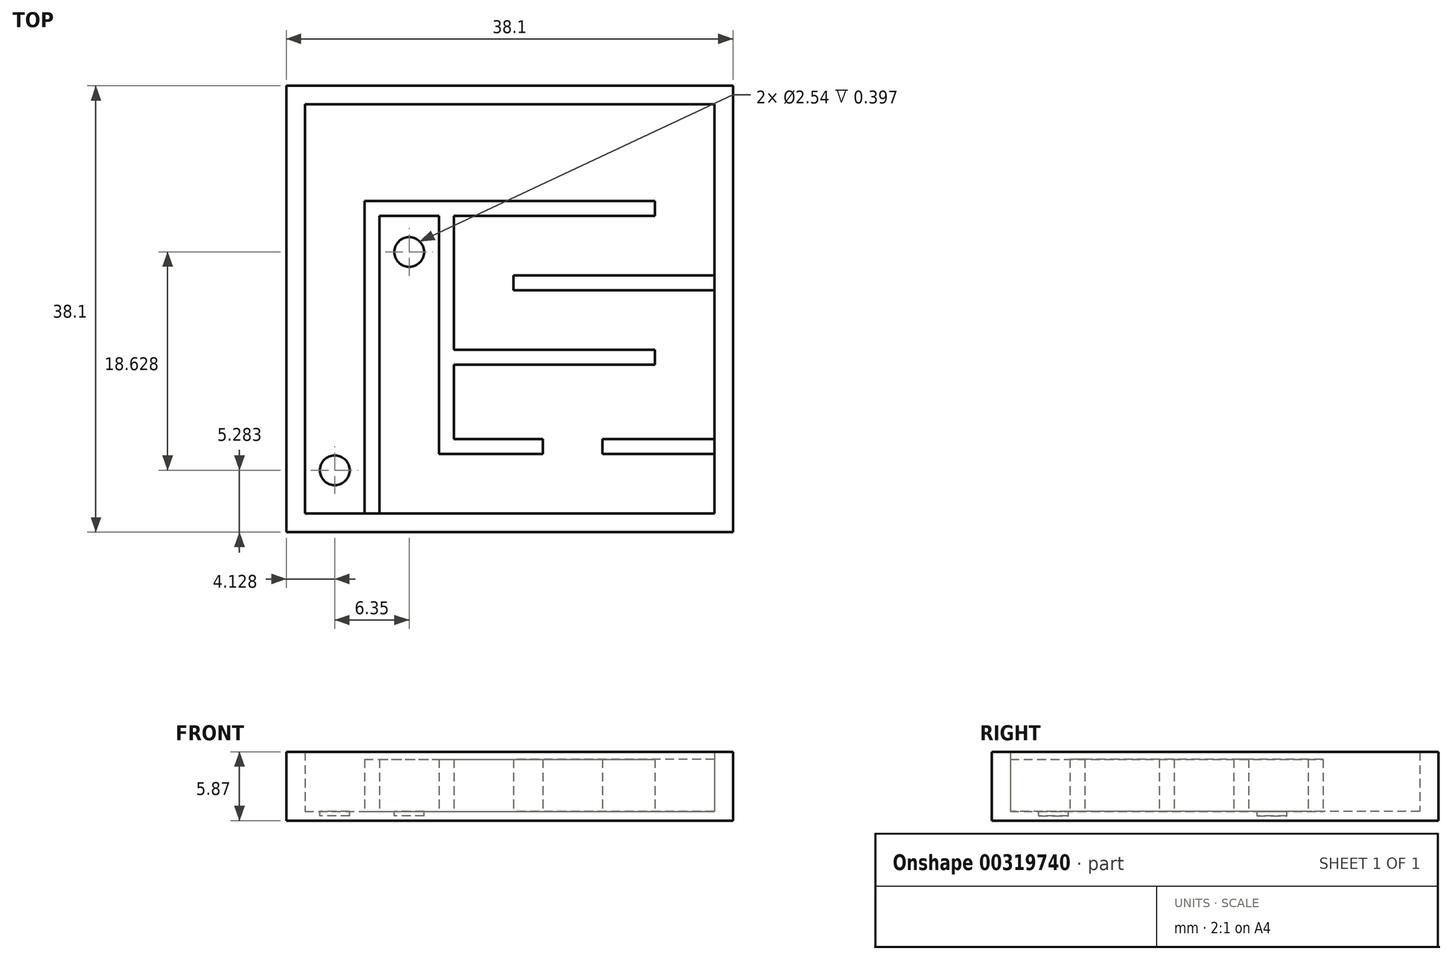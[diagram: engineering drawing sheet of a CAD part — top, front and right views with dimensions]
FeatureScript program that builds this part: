
annotation { "Feature Type Name" : "Feature", "Feature Type Description" : "" }
export const myFeature = defineFeature(function(context is Context, id is Id, definition is map)
    precondition{}
    {
        {
            var Q0;
            Q0=qCreatedBy(makeId("Top.planeOp"),FACE);
            var sketch = newSketch(context, id + "F0", { "sketchPlane" : qUnion([Q0])});
            skLineSegment(sketch, "E0.bottom", {"start": v(-12.95, 15.4) * mm, "end": v(25.15, 15.4) * mm});
            skLineSegment(sketch, "E0.top", {"start": v(-12.95, -22.7) * mm, "end": v(25.15, -22.7) * mm});
            skLineSegment(sketch, "E0.left", {"start": v(-12.95, 15.4) * mm, "end": v(-12.95, -22.7) * mm});
            skLineSegment(sketch, "E0.right", {"start": v(25.15, 15.4) * mm, "end": v(25.15, -22.7) * mm});
            skSolve(sketch);
        }
        {
            var Q0;
            Q0=makeQuery(id+"F0.imprint","IMPRINT",FACE,{"disambiguationData":[TD([[makeQuery(id+"F0.imprint","IMPRINT",EDGE,{"derivedFrom":sQuery(id+"F0.wireOp",EDGE,"E0.bottom")}),-1.0]])]});
            extrude(context, id + "F1", {"entities" : qUnion([Q0]), "depth" : 0.8 * mm});
        }
        {
            var Q0;
            Q0=makeQuery(id+"F1.opExtrude","CAP_FACE",FACE,{"disambiguationData":[OSD([sQuery(id+"F0.wireOp",EDGE,"E0.bottom"),sQuery(id+"F0.wireOp",EDGE,"E0.top"),sQuery(id+"F0.wireOp",EDGE,"E0.left"),sQuery(id+"F0.wireOp",EDGE,"E0.right")])],"isStart":false});
            var sketch = newSketch(context, id + "F2", { "sketchPlane" : qUnion([Q0])});
            skLineSegment(sketch, "E1.0", {"start": v(-11.36, 13.8) * mm, "end": v(23.56, 13.8) * mm});
            skLineSegment(sketch, "E1.1", {"start": v(-11.36, 13.8) * mm, "end": v(-11.36, -21.12) * mm});
            skLineSegment(sketch, "E1.2", {"start": v(-11.36, -21.12) * mm, "end": v(23.56, -21.12) * mm});
            skLineSegment(sketch, "E1.3", {"start": v(23.56, 13.8) * mm, "end": v(23.56, -21.12) * mm});
            skSolve(sketch);
        }
        {
            var Q0;
            Q0=makeQuery(id+"F2.imprint","IMPRINT",FACE,{"disambiguationData":[TD([[makeQuery(id+"F2.imprint","IMPRINT",EDGE,{"derivedFrom":sQuery(id+"F2.wireOp",EDGE,"E1.0")}),1.0]])]});
            extrude(context, id + "F3", {"entities" : qUnion([Q0]), "operationType" : NewBodyOperationType.ADD, "depth" : 5.08 * mm});
        }
        {
            var Q0;
            Q0=makeQuery(id+"F1.opExtrude","CAP_FACE",FACE,{"disambiguationData":[OSD([sQuery(id+"F0.wireOp",EDGE,"E0.bottom"),sQuery(id+"F0.wireOp",EDGE,"E0.top"),sQuery(id+"F0.wireOp",EDGE,"E0.left"),sQuery(id+"F0.wireOp",EDGE,"E0.right")])],"isStart":false});
            var sketch = newSketch(context, id + "F4", { "sketchPlane" : qUnion([Q0])});
            skLineSegment(sketch, "E2.bottom", {"start": v(-6.28, -21.12) * mm, "end": v(-5.01, -21.12) * mm});
            skLineSegment(sketch, "E2.top", {"start": v(-6.28, 5.55) * mm, "end": v(-5.01, 5.55) * mm});
            skLineSegment(sketch, "E2.left", {"start": v(-6.28, -21.12) * mm, "end": v(-6.28, 5.55) * mm});
            skLineSegment(sketch, "E2.right", {"start": v(-5.01, -21.12) * mm, "end": v(-5.01, 4.28) * mm});
            skLineSegment(sketch, "E3.bottom", {"start": v(-5.01, 5.55) * mm, "end": v(18.48, 5.55) * mm});
            skLineSegment(sketch, "E3.top", {"start": v(-5.01, 4.28) * mm, "end": v(0.07, 4.28) * mm});
            skLineSegment(sketch, "E3.right", {"start": v(18.48, 5.55) * mm, "end": v(18.48, 4.28) * mm});
            skLineSegment(sketch, "E4.left", {"start": v(0.07, 4.28) * mm, "end": v(0.07, -16.04) * mm});
            skLineSegment(sketch, "E4.right", {"start": v(1.34, 4.28) * mm, "end": v(1.34, -7.15) * mm});
            skLineSegment(sketch, "E5.bottom", {"start": v(1.34, -7.15) * mm, "end": v(18.48, -7.15) * mm});
            skLineSegment(sketch, "E5.top", {"start": v(1.34, -8.42) * mm, "end": v(18.48, -8.42) * mm});
            skLineSegment(sketch, "E5.right", {"start": v(18.48, -7.15) * mm, "end": v(18.48, -8.42) * mm});
            skLineSegment(sketch, "E6.top", {"start": v(1.34, -14.77) * mm, "end": v(8.93, -14.77) * mm});
            skLineSegment(sketch, "E6.right", {"start": v(8.93, -16.04) * mm, "end": v(8.93, -14.77) * mm});
            skLineSegment(sketch, "E7.right", {"start": v(14.01, -18.58) * mm, "end": v(14.01, -18.58) * mm});
            skLineSegment(sketch, "E8.bottom", {"start": v(23.56, -0.8) * mm, "end": v(6.42, -0.8) * mm});
            skLineSegment(sketch, "E8.top", {"start": v(23.56, -2.07) * mm, "end": v(6.42, -2.07) * mm});
            skLineSegment(sketch, "E8.left", {"start": v(23.56, -0.8) * mm, "end": v(23.56, -2.07) * mm});
            skLineSegment(sketch, "E8.right", {"start": v(6.42, -0.8) * mm, "end": v(6.42, -2.07) * mm});
            skLineSegment(sketch, "E9.left", {"start": v(7.18, -16.04) * mm, "end": v(7.18, -16.04) * mm});
            skLineSegment(sketch, "E9.right", {"start": v(8.93, -14.77) * mm, "end": v(8.93, -16.04) * mm});
            skLineSegment(sketch, "E10.trimOffspring", {"start": v(1.34, -8.42) * mm, "end": v(1.34, -14.77) * mm});
            skLineSegment(sketch, "E11.trimOffspring", {"start": v(1.34, 4.28) * mm, "end": v(18.48, 4.28) * mm});
            skLineSegment(sketch, "E12", {"start": v(23.56, -0.8) * mm, "end": v(23.56, -0.8) * mm});
            skLineSegment(sketch, "E13", {"start": v(6.42, -0.8) * mm, "end": v(6.42, -0.8) * mm});
            skLineSegment(sketch, "E14", {"start": v(6.42, -0.8) * mm, "end": v(23.56, -0.8) * mm});
            skPoint(sketch, "E4.top.end.orphan", {"position": v(1.34, -18.58) * mm});
            skLineSegment(sketch, "E15", {"start": v(0.07, -16.04) * mm, "end": v(8.93, -16.04) * mm});
            skLineSegment(sketch, "E16.bottom", {"start": v(23.56, -14.77) * mm, "end": v(14.01, -14.77) * mm});
            skLineSegment(sketch, "E16.top", {"start": v(23.56, -16.04) * mm, "end": v(14.01, -16.04) * mm});
            skLineSegment(sketch, "E16.left", {"start": v(23.56, -14.77) * mm, "end": v(23.56, -16.04) * mm});
            skLineSegment(sketch, "E16.right", {"start": v(14.01, -14.77) * mm, "end": v(14.01, -16.04) * mm});
            skLineSegment(sketch, "E17", {"start": v(-11.36, -21.12) * mm, "end": v(-6.28, -21.12) * mm});
            skCircle(sketch, "E18", {"center": v(-8.82, -17.43) * mm, "radius": 1.27 * mm});
            skPoint(sketch, "E18.centerSnap0", {"position": v(-8.82, -21.12) * mm});
            skCircle(sketch, "E19", {"center": v(-2.47, 1.2) * mm, "radius": 1.27 * mm});
            skPoint(sketch, "E19.centerSnap0", {"position": v(-2.47, 4.28) * mm});
            skSolve(sketch);
        }
        {
            var Q0;
            Q0=makeQuery(id+"F4.imprint","IMPRINT",FACE,{"disambiguationData":[TD([[makeQuery(id+"F4.imprint","IMPRINT",EDGE,{"derivedFrom":sQuery(id+"F4.wireOp",EDGE,"E2.bottom")}),1.0]])]});
            var Q1;
            Q1=makeQuery(id+"F4.imprint","IMPRINT",FACE,{"disambiguationData":[TD([[makeQuery(id+"F4.imprint","IMPRINT",EDGE,{"derivedFrom":sQuery(id+"F4.wireOp",EDGE,"E8.top")}),-1.0]])]});
            var Q2;
            Q2=makeQuery(id+"F4.imprint","IMPRINT",FACE,{"disambiguationData":[TD([[makeQuery(id+"F4.imprint","IMPRINT",EDGE,{"derivedFrom":sQuery(id+"F4.wireOp",EDGE,"E16.bottom")}),1.0]])]});
            extrude(context, id + "F5", {"entities" : qUnion([Q0, Q1, Q2]), "operationType" : NewBodyOperationType.ADD, "depth" : 4.44 * mm});
        }
        {
            var Q0;
            Q0=makeQuery(id+"F4.imprint","IMPRINT",FACE,{"disambiguationData":[TD([[makeQuery(id+"F4.imprint","IMPRINT",EDGE,{"derivedFrom":sQuery(id+"F4.wireOp",EDGE,"E18")}),1.0]])]});
            var Q1;
            Q1=makeQuery(id+"F4.imprint","IMPRINT",FACE,{"disambiguationData":[TD([[makeQuery(id+"F4.imprint","IMPRINT",EDGE,{"derivedFrom":sQuery(id+"F4.wireOp",EDGE,"E19")}),1.0]])]});
            extrude(context, id + "F6", {"entities" : qUnion([Q0, Q1]), "operationType" : NewBodyOperationType.REMOVE, "oppositeDirection" : true, "depth" : 0.4 * mm});
        }
    });
